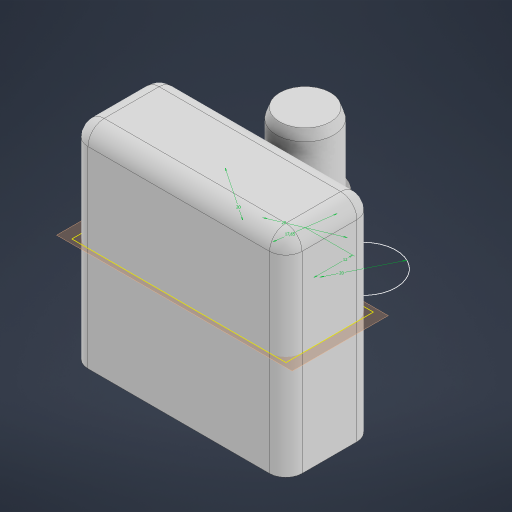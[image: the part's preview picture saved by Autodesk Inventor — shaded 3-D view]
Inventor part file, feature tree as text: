
AUTODESK INVENTOR PART (.ipt)
format: ipt  version: 2023 (Build 270158000, 158)  size: 250,368 bytes
history: native  units: mm
features: extrude x4, sketch x2, fillet x2, chamfer x2, plane x1, projected_geometry x1
ambient origin geometry x8: Origin, YZ Plane, XZ Plane, XY Plane, X Axis, Y Axis, Z Axis, Center Point
bodies: Solid1 (feature_tree)
feature tree (12):
  sketch  "Sketch1"  dims[d0=26.9mm d1=65.9mm]
  extrude  "Extrusion1"  Depth=65.9mm
  extrude  "Extrusion2"  Depth=24.5mm
  fillet  "Fillet1"  Radius=63.5mm
  plane  "Work Plane1"
  sketch  "Sketch3"  dims[d2=1.2mm d3=24.5mm d4=63.5mm d5=1.2mm d6=0.0mm d7=63.0mm d8=0.0mm d9=5.0mm d10=17.65mm d11=20.0mm d12=12.0mm d13=20.0mm d14=20.0mm d15=20.0mm d16=0.0mm d17=64.2mm d18=0.0mm d19=1.0mm d20=3.0mm d21=45.0deg d22=1.0mm d23=3.0mm d24=45.0deg d25=5.0mm]
  extrude  "Extrusion3"  Depth=1.2mm TaperAngle=0.0deg
  extrude  "Extrusion4"  Depth=63.0mm TaperAngle=0.0deg
  chamfer  "Chamfer1"  Distance=5.0mm
  chamfer  "Chamfer2"  Distance=17.65mm
  fillet  "Fillet2"  Radius=20.0mm
  projected_geometry  "Project Cut Edges1"
